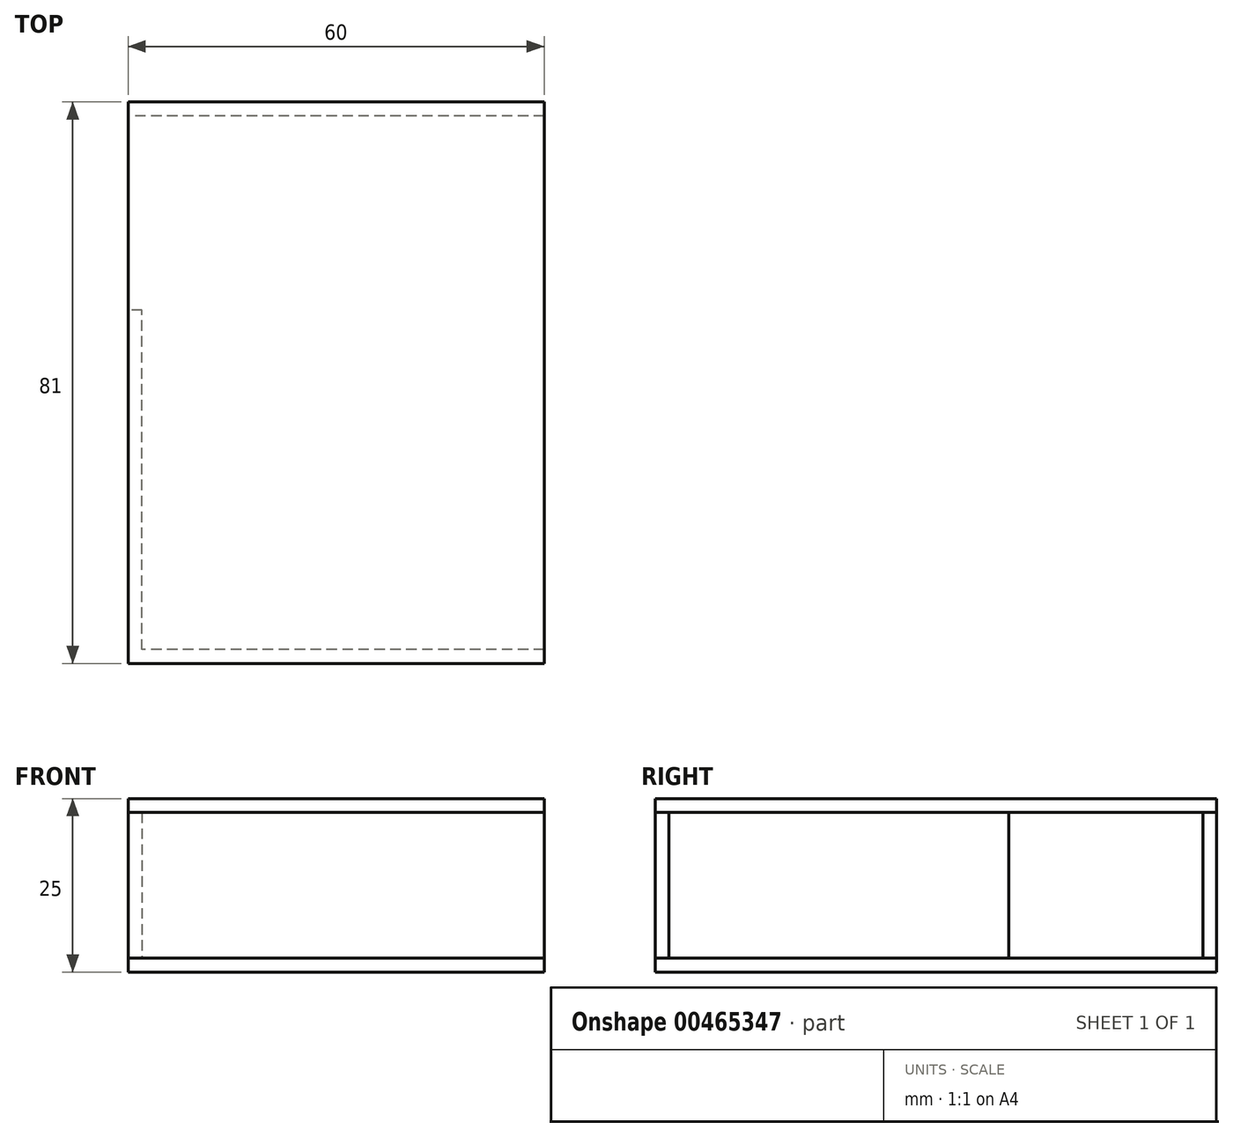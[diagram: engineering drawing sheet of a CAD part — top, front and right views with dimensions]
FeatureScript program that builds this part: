
annotation { "Feature Type Name" : "Feature", "Feature Type Description" : "" }
export const myFeature = defineFeature(function(context is Context, id is Id, definition is map)
    precondition{}
    {
        {
            var Q0;
            Q0=qCreatedBy(makeId("Top.planeOp"),FACE);
            var sketch = newSketch(context, id + "F0", { "sketchPlane" : qUnion([Q0])});
            skLineSegment(sketch, "E0", {"start": v(0, 0) * mm, "end": v(60, 0) * mm});
            skLineSegment(sketch, "E1", {"start": v(60, 0) * mm, "end": v(60, 81) * mm});
            skLineSegment(sketch, "E2", {"start": v(60, 81) * mm, "end": v(0, 81) * mm});
            skLineSegment(sketch, "E3", {"start": v(0, 81) * mm, "end": v(0, 0) * mm});
            skSolve(sketch);
        }
        {
            var Q0;
            Q0=makeQuery(id+"F0.imprint","IMPRINT",FACE,{"disambiguationData":[TD([[makeQuery(id+"F0.imprint","IMPRINT",EDGE,{"derivedFrom":sQuery(id+"F0.wireOp",EDGE,"E0")}),1.0]])]});
            extrude(context, id + "F1", {"entities" : qUnion([Q0]), "oppositeDirection" : true, "depth" : 2 * mm});
        }
        {
            var Q0;
            Q0=qCreatedBy(makeId("Top.planeOp"),FACE);
            var sketch = newSketch(context, id + "F2", { "sketchPlane" : qUnion([Q0])});
            skLineSegment(sketch, "E4", {"start": v(0, 0) * mm, "end": v(60, 0) * mm});
            skLineSegment(sketch, "E5", {"start": v(60, 0) * mm, "end": v(60, 2) * mm});
            skLineSegment(sketch, "E6", {"start": v(60, 2) * mm, "end": v(2, 2) * mm});
            skLineSegment(sketch, "E7", {"start": v(2, 2) * mm, "end": v(2, 51) * mm});
            skLineSegment(sketch, "E8", {"start": v(2, 51) * mm, "end": v(0, 51) * mm});
            skLineSegment(sketch, "E9", {"start": v(0, 51) * mm, "end": v(0, 0) * mm});
            skLineSegment(sketch, "E10", {"start": v(0, 81) * mm, "end": v(60, 81) * mm});
            skLineSegment(sketch, "E11", {"start": v(60, 81) * mm, "end": v(60, 79) * mm});
            skLineSegment(sketch, "E12", {"start": v(60, 79) * mm, "end": v(0, 79) * mm});
            skLineSegment(sketch, "E13", {"start": v(0, 79) * mm, "end": v(0, 81) * mm});
            skSolve(sketch);
        }
        {
            var Q0;
            Q0=qCreatedBy(makeId("Top.planeOp"),FACE);
            cPlane(context, id + "F3", {"entities" : qUnion([Q0]), "cplaneType" : CPlaneType.OFFSET, "offset" : 21 * mm, "width" : 150 * mm, "height" : 150 * mm});
        }
        {
            var Q0;
            Q0=qCreatedBy(makeId("Front.planeOp"),FACE);
            var sketch = newSketch(context, id + "F4", { "sketchPlane" : qUnion([Q0])});
            skLineSegment(sketch, "E14", {"start": v(0, 21) * mm, "end": v(60, 21) * mm});
            skLineSegment(sketch, "E15", {"start": v(60, 21) * mm, "end": v(60, 23) * mm});
            skLineSegment(sketch, "E16", {"start": v(60, 23) * mm, "end": v(0, 23) * mm});
            skLineSegment(sketch, "E17", {"start": v(0, 23) * mm, "end": v(0, 21) * mm});
            skSolve(sketch);
        }
        {
            var Q0;
            Q0=makeQuery(id+"F2.imprint","IMPRINT",FACE,{"disambiguationData":[TD([[makeQuery(id+"F2.imprint","IMPRINT",EDGE,{"derivedFrom":sQuery(id+"F2.wireOp",EDGE,"E4")}),1.0]])]});
            var Q1;
            Q1=makeQuery(id+"F2.imprint","IMPRINT",FACE,{"disambiguationData":[TD([[makeQuery(id+"F2.imprint","IMPRINT",EDGE,{"derivedFrom":sQuery(id+"F2.wireOp",EDGE,"E10")}),-1.0]])]});
            var Q2;
            Q2=sQuery(id+"F2.wireOp",EDGE,"E10");
            var Q3;
            Q3=sQuery(id+"F2.wireOp",EDGE,"E4");
            var Q4;
            Q4=sQuery(id+"F2.wireOp",EDGE,"E6");
            var Q5;
            Q5=sQuery(id+"F2.wireOp",EDGE,"E12");
            var Q6;
            Q6=sQuery(id+"F2.wireOp",EDGE,"E9");
            var Q7;
            Q7=sQuery(id+"F2.wireOp",EDGE,"E7");
            var Q8;
            Q8=sQuery(id+"F2.wireOp",EDGE,"E5");
            var Q9;
            Q9=sQuery(id+"F2.wireOp",EDGE,"E8");
            var Q10;
            Q10=sQuery(id+"F2.wireOp",EDGE,"E11");
            var Q11;
            Q11=sQuery(id+"F2.wireOp",EDGE,"E13");
            extrude(context, id + "F5", {"entities" : qUnion([Q0, Q1]), "surfaceEntities" : qUnion([Q2, Q3, Q4, Q5, Q6, Q7, Q8, Q9, Q10, Q11]), "depth" : 21 * mm});
        }
        {
            var Q0;
            Q0=makeQuery(id+"F4.imprint","IMPRINT",FACE,{"disambiguationData":[TD([[makeQuery(id+"F4.imprint","IMPRINT",EDGE,{"derivedFrom":sQuery(id+"F4.wireOp",EDGE,"E14")}),1.0]])]});
            var Q1;
            Q1=sQuery(id+"F4.wireOp",EDGE,"E16");
            var Q2;
            Q2=sQuery(id+"F4.wireOp",EDGE,"E14");
            var Q3;
            Q3=sQuery(id+"F4.wireOp",EDGE,"E17");
            var Q4;
            Q4=sQuery(id+"F4.wireOp",EDGE,"E15");
            extrude(context, id + "F6", {"entities" : qUnion([Q0]), "surfaceEntities" : qUnion([Q1, Q2, Q3, Q4]), "oppositeDirection" : true, "depth" : 81 * mm});
        }
    });
